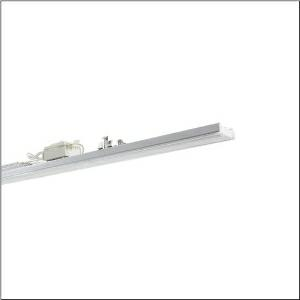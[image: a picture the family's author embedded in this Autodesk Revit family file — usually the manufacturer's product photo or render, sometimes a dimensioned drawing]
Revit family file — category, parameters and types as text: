
# Revit family: licross_11_recessed_ho_51tl12mn4exm
name_source: partatom
category: Lighting Fixtures
units: mm (PartAtom-declared; Revit-internal decimal feet)

## family parameters
Cut with Voids When Loaded = No
Host = Face
Light Source = No
Part Type = Normal
Room Calculation Point = No
Round Connector Dimension = Use Diameter
Shared = No

## types (1)
- --- (1 x LED, 14100 lm, 74.5 W, 4000K)
    Apparent Load = 75 VA
    CIE Flux Codes = 66 91 98 100 100
    Color Rendering = 80
    Color Temperature = 4000K
    Default Elevation = 1800 mm
    Description = Licross 11 Recessed HO, luminaire insert, of sheet steel, coil coated, white, length: 1.500mm, width: 66mm, height: 67mm, LED rated luminous flux: 14.100lm, light colour: 840, SDCM (Standard Deviation of Colour Matching)MacAdam ≤ 2 SDCM (initial), control gear: ON/OFF Multilumen, with plug, 3-pole, with phase selection, mains connection: 220..240V, AC, 50/60Hz, rated input power: 75W, internal wiring halogen-free, primary optical cover: cover, of PMMA, light emission: direct distribution, primary light characteristic: symmetric, protection rating (complete): IP40, insulation class (complete): insulation class I (protective earthing), certification: CE, ENEC, VDE, UKCA, protection symbol: D if used in an environment without relevant dust loads with corresponding accessories, impact resistance: IK06, permissible ambient temperature for indoor applications: -35..+35°C, corresponds to IFS (International Featured Standards) requirements for safety and quality in the food industry, reducing of maximum allowable ambient temperature of 5°C with ceiling mounting, The light source and the operating device comply with the requirements of the Ecodesign Regulation (EU) 2019/2020 and are replaceable in accordance with this regulation, packaging unit: 1 piece
    Height = 58 mm
    Lamp = 1 x LED
    Lamp Light Flux = 14100 lm
    Lamp Power = 74.5 W
    Lamp count = 1
    Length = 1500 mm
    Luminous efficacy = 189 lm/W
    Manufacturer = Siteco
    ModVariant = No
    Model = 51TL12MN4EXM
    Mounting Place = Ceiling
    Mounting Type = Pendant
    Number of Poles = 1
    OnlyDefault = Yes
    Power Factor = 1
    Product Name = Licross 11 Recessed HO
    Product group = luminaire insert | ceiling pendant
    ProductGroupID = 901
    Protection Class = Protection class I
    Protection Degree = IP 40
    RLX_Detail_Level = 1
    RLX_Emergency_Light_Flux = 0 lm
    RLX_Emergency_Type = 0
    RLX_Emergency_Type_DB = No
    RlxData = <blob elided: 22385 chars, md5=697001c4>
    Socket = socket
    Standby Power = 0 W
    System Light Flux = 14100 lm
    System Power = 75 W
    Type Comments = factory setting: luminous flux: 100 % | (A | C | E) | 174 mA
    Type Image = l_1296930.jpg
    URL = http://relux.com
    VarID = @adj_089927
    Voltage = 0 V
    Weight = 0.00 kg
    Width = 66 mm

## geometry (parser evidence)
native form markers: Blend x4, Sweep x11
no freeform markers — native parametric forms only
